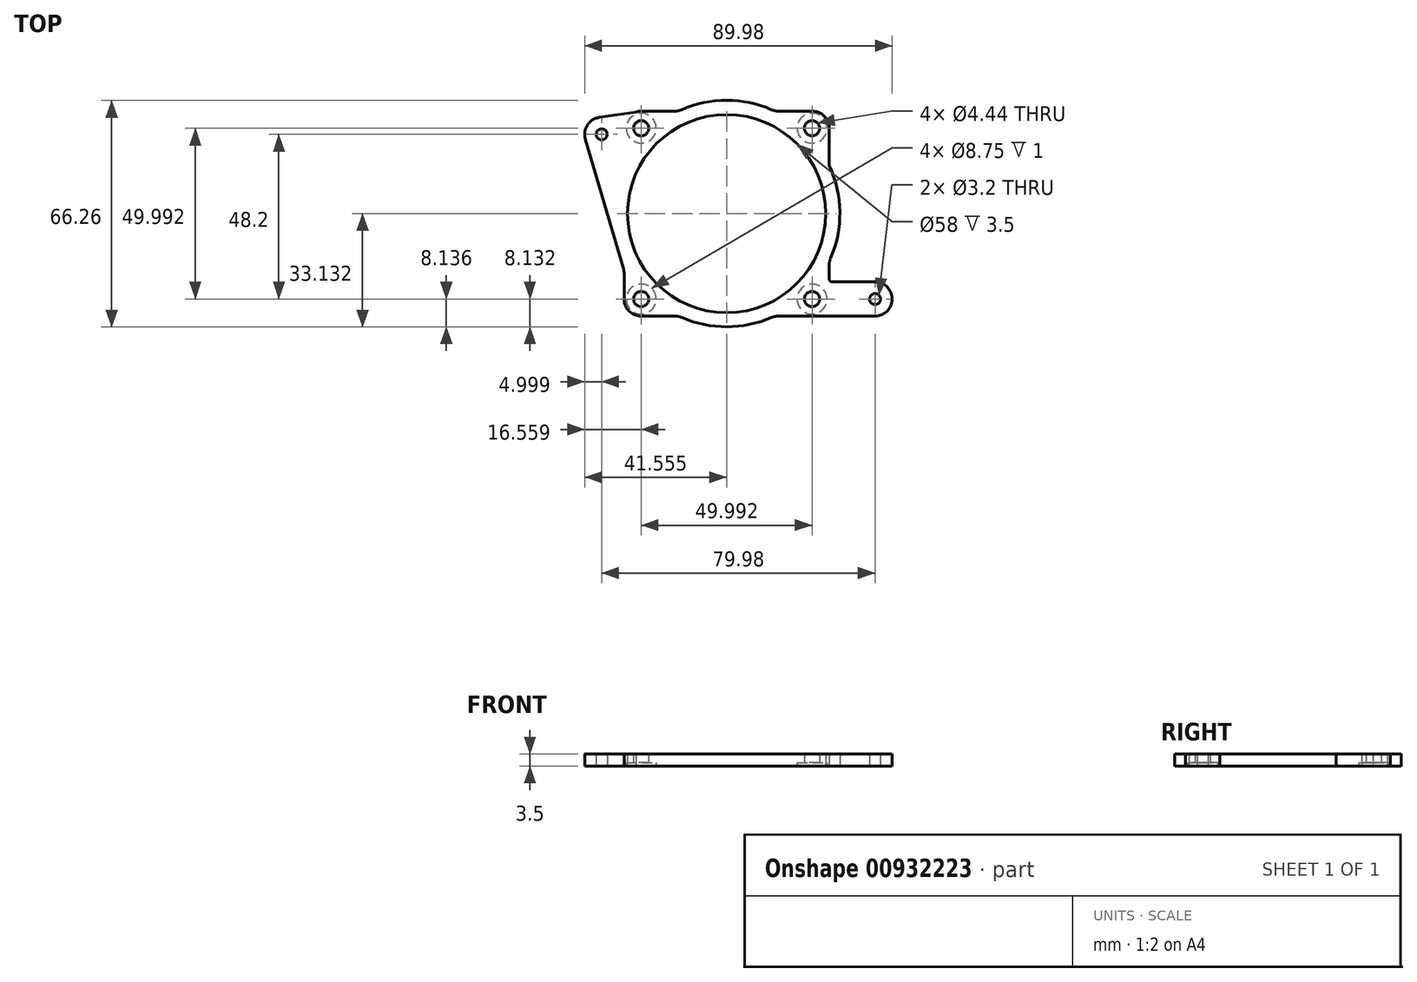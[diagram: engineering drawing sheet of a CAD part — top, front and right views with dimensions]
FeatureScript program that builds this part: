
annotation { "Feature Type Name" : "Feature", "Feature Type Description" : "" }
export const myFeature = defineFeature(function(context is Context, id is Id, definition is map)
    precondition{}
    {
        {
            var Q0;
            Q0=qCreatedBy(makeId("Top.planeOp"),FACE);
            var sketch = newSketch(context, id + "F0", { "sketchPlane" : qUnion([Q0])});
            skLineSegment(sketch, "E0.bottom", {"start": v(-53.42, 44.82) * mm, "end": v(48.18, 44.82) * mm, "construction": true});
            skLineSegment(sketch, "E0.top", {"start": v(-53.42, -8.48) * mm, "end": v(48.18, -8.48) * mm, "construction": true});
            skLineSegment(sketch, "E0.left", {"start": v(-53.42, 44.82) * mm, "end": v(-53.42, -8.48) * mm, "construction": true});
            skLineSegment(sketch, "E0.right", {"start": v(48.18, 44.82) * mm, "end": v(48.18, -8.48) * mm, "construction": true});
            skCircle(sketch, "E1", {"center": v(-39.42, -5.98) * mm, "radius": 1.6 * mm, "construction": true});
            skCircle(sketch, "E2", {"center": v(-38.12, 42.22) * mm, "radius": 1.6 * mm});
            skCircle(sketch, "E3", {"center": v(36.78, 42.22) * mm, "radius": 1.6 * mm, "construction": true});
            skCircle(sketch, "E4", {"center": v(41.86, -5.98) * mm, "radius": 1.6 * mm});
            skCircle(sketch, "E5", {"center": v(12.68, -0.88) * mm, "radius": 1.6 * mm, "construction": true});
            skCircle(sketch, "E6", {"center": v(12.68, 27.02) * mm, "radius": 1.6 * mm, "construction": true});
            skLineSegment(sketch, "E7.bottom", {"start": v(-26.56, 49.02) * mm, "end": v(-16.7, 49.02) * mm});
            skLineSegment(sketch, "E7.top", {"start": v(-26.56, -10.98) * mm, "end": v(-16.7, -10.98) * mm});
            skLineSegment(sketch, "E7.left", {"start": v(-31.56, 1.62) * mm, "end": v(-31.56, -5.98) * mm});
            skLineSegment(sketch, "E7.right", {"start": v(28.44, 44.02) * mm, "end": v(28.44, 33.08) * mm});
            skCircle(sketch, "E8", {"center": v(-26.56, 44.02) * mm, "radius": 2.22 * mm});
            skLineSegment(sketch, "E9", {"start": v(-31.56, 49.02) * mm, "end": v(28.44, -10.98) * mm, "construction": true});
            skLineSegment(sketch, "E10", {"start": v(28.44, 49.02) * mm, "end": v(-31.56, -10.98) * mm, "construction": true});
            skArc(sketch, "E11", {"start": v(-22.35, 44.82) * mm, "mid": v(-34.66, 17.59) * mm, "end": v(-20.04, -8.48) * mm, "construction": true});
            skCircle(sketch, "E12", {"center": v(23.43, 44.02) * mm, "radius": 2.22 * mm});
            skCircle(sketch, "E13", {"center": v(23.43, -5.97) * mm, "radius": 2.22 * mm});
            skCircle(sketch, "E14", {"center": v(-26.56, -5.97) * mm, "radius": 2.22 * mm});
            skPoint(sketch, "E15.visualSharp", {"position": v(28.44, 49.02) * mm});
            skArc(sketch, "E15.filletArc", {"start": v(28.44, 44.02) * mm, "mid": v(26.97, 47.56) * mm, "end": v(23.44, 49.02) * mm});
            skPoint(sketch, "E16.visualSharp", {"position": v(28.44, -10.98) * mm});
            skLineSegment(sketch, "E16.filletArc", {"start": v(23.44, -10.98) * mm, "end": v(23.44, -10.98) * mm});
            skPoint(sketch, "E17.visualSharp", {"position": v(-31.56, -10.98) * mm});
            skArc(sketch, "E17.filletArc", {"start": v(-31.56, -5.98) * mm, "mid": v(-30.1, -9.51) * mm, "end": v(-26.56, -10.98) * mm});
            skPoint(sketch, "E18.visualSharp", {"position": v(-31.56, 49.02) * mm});
            skArc(sketch, "E18.filletArc", {"start": v(-26.56, 49.02) * mm, "mid": v(-28.48, 48.64) * mm, "end": v(-30.1, 47.56) * mm});
            skPoint(sketch, "E19.19", {"position": v(-146.14, 42.5) * mm});
            skPoint(sketch, "E20.0", {"position": v(-66.16, -5.7) * mm});
            skPoint(sketch, "E21", {"position": v(-1.56, 17.8) * mm});
            skCircle(sketch, "E22", {"center": v(-1.56, 19.02) * mm, "radius": 29 * mm});
            skArc(sketch, "E23", {"start": v(-38.87, 47.17) * mm, "mid": v(-42.34, 44.9) * mm, "end": v(-42.92, 40.8) * mm});
            skLineSegment(sketch, "E24", {"start": v(-31.77, 3.04) * mm, "end": v(-42.92, 40.8) * mm});
            skLineSegment(sketch, "E25", {"start": v(-26.56, 49.02) * mm, "end": v(-38.87, 47.17) * mm});
            skLineSegment(sketch, "E26", {"start": v(41.86, -10.98) * mm, "end": v(23.44, -10.98) * mm});
            skPoint(sketch, "E27.visualSharp", {"position": v(46.86, 15.79) * mm});
            skLineSegment(sketch, "E28", {"start": v(37.65, 11.98) * mm, "end": v(37.65, 37.31) * mm, "construction": true});
            skLineSegment(sketch, "E29", {"start": v(37.65, 11.98) * mm, "end": v(37.65, -33.07) * mm, "construction": true});
            skArc(sketch, "E30.filletArc", {"start": v(-31.56, 1.62) * mm, "mid": v(-31.62, 2.33) * mm, "end": v(-31.77, 3.04) * mm});
            skArc(sketch, "E31.trimOffspring", {"start": v(37.53, -8.48) * mm, "mid": v(37.59, -8.58) * mm, "end": v(37.65, -8.67) * mm});
            skPoint(sketch, "E32.orphan", {"position": v(28.44, -5.98) * mm});
            skPoint(sketch, "E33.visualSharp", {"position": v(28.44, 35.44) * mm});
            skArc(sketch, "E34.trimOffspring", {"start": v(11.58, 49.43) * mm, "mid": v(-1.56, 52.15) * mm, "end": v(-14.71, 49.43) * mm});
            skArc(sketch, "E35.trimOffspring", {"start": v(-14.71, -11.39) * mm, "mid": v(-1.56, -14.1) * mm, "end": v(11.58, -11.39) * mm});
            skArc(sketch, "E36.trimOffspring", {"start": v(16.91, -8.48) * mm, "mid": v(21.2, -5.06) * mm, "end": v(24.85, -0.98) * mm, "construction": true});
            skLineSegment(sketch, "E37.trimOffspring", {"start": v(13.56, 49.02) * mm, "end": v(23.44, 49.02) * mm});
            skPoint(sketch, "E38.visualSharp", {"position": v(-15.62, 49.02) * mm});
            skArc(sketch, "E38.filletArc", {"start": v(-16.7, 49.02) * mm, "mid": v(-15.68, 49.13) * mm, "end": v(-14.71, 49.43) * mm});
            skPoint(sketch, "E39.visualSharp", {"position": v(12.5, 49.02) * mm});
            skArc(sketch, "E39.filletArc", {"start": v(11.58, 49.43) * mm, "mid": v(12.55, 49.13) * mm, "end": v(13.56, 49.02) * mm});
            skLineSegment(sketch, "E40.trimOffspring", {"start": v(13.56, -10.98) * mm, "end": v(23.44, -10.98) * mm});
            skPoint(sketch, "E41.visualSharp", {"position": v(-15.62, -10.98) * mm});
            skArc(sketch, "E41.filletArc", {"start": v(-14.71, -11.39) * mm, "mid": v(-15.68, -11.08) * mm, "end": v(-16.7, -10.98) * mm});
            skPoint(sketch, "E42.visualSharp", {"position": v(12.5, -10.98) * mm});
            skArc(sketch, "E42.filletArc", {"start": v(13.56, -10.98) * mm, "mid": v(12.55, -11.08) * mm, "end": v(11.58, -11.39) * mm});
            skCircle(sketch, "E43.converted", {"center": v(41.86, -5.98) * mm, "radius": 5 * mm});
            skLineSegment(sketch, "E44", {"start": v(41.86, -0.98) * mm, "end": v(29.44, -0.98) * mm});
            skLineSegment(sketch, "E45", {"start": v(24.85, -0.98) * mm, "end": v(24.85, -0.98) * mm});
            skLineSegment(sketch, "E46", {"start": v(28.44, 3.9) * mm, "end": v(28.44, 0.02) * mm});
            skArc(sketch, "E47.trimOffspring", {"start": v(28.85, 5.88) * mm, "mid": v(30.6, 26.97) * mm, "end": v(19.22, 44.82) * mm});
            skPoint(sketch, "E48.visualSharp", {"position": v(28.44, -0.98) * mm});
            skArc(sketch, "E48.filletArc", {"start": v(28.44, 0.02) * mm, "mid": v(28.73, -0.69) * mm, "end": v(29.44, -0.98) * mm});
            skPoint(sketch, "E49.visualSharp", {"position": v(28.44, 4.96) * mm});
            skArc(sketch, "E49.filletArc", {"start": v(28.85, 5.88) * mm, "mid": v(28.54, 4.9) * mm, "end": v(28.44, 3.9) * mm});
            skSolve(sketch);
        }
        {
            var Q0;
            Q0=qCreatedBy(makeId("Top.planeOp"),FACE);
            cPlane(context, id + "F1", {"entities" : qUnion([Q0]), "cplaneType" : CPlaneType.OFFSET, "offset" : 5 * mm, "oppositeDirection" : true, "width" : 150 * mm, "height" : 150 * mm});
        }
        {
            var Q0;
            Q0 = qSketchRegion(id + "F0", true);
            extrude(context, id + "F2", {"entities" : qUnion([Q0]), "depth" : 3.5 * mm, "offsetDistance" : 25 * mm});
        }
        {
            var Q0;
            Q0=makeQuery(id+"F2.opExtrude","CAP_FACE",FACE,{"disambiguationData":[OSD([sQuery(id+"F0.wireOp",EDGE,"E2"),sQuery(id+"F0.wireOp",EDGE,"E4"),sQuery(id+"F0.wireOp",EDGE,"E7.bottom"),sQuery(id+"F0.wireOp",EDGE,"E7.top"),sQuery(id+"F0.wireOp",EDGE,"E7.left"),sQuery(id+"F0.wireOp",EDGE,"E7.right"),sQuery(id+"F0.wireOp",EDGE,"E8"),sQuery(id+"F0.wireOp",EDGE,"E12"),sQuery(id+"F0.wireOp",EDGE,"E13"),sQuery(id+"F0.wireOp",EDGE,"E14"),sQuery(id+"F0.wireOp",EDGE,"E15.filletArc"),sQuery(id+"F0.wireOp",EDGE,"E17.filletArc"),sQuery(id+"F0.wireOp",EDGE,"E18.filletArc"),sQuery(id+"F0.wireOp",EDGE,"E22"),sQuery(id+"F0.wireOp",EDGE,"E23"),sQuery(id+"F0.wireOp",EDGE,"curC7CVh-JOHb-7Mg7-MYZK-eGtlUkxcjdBB"),sQuery(id+"F0.wireOp",EDGE,"E24"),sQuery(id+"F0.wireOp",EDGE,"E25"),sQuery(id+"F0.wireOp",EDGE,"E26"),sQuery(id+"F0.wireOp",EDGE,"FxnBB36o-Rqyz-MdkS-9HdU-SdkZIjoqN9XQ"),sQuery(id+"F0.wireOp",EDGE,"PDu09gB8-Ofy4-FQeL-J0Lt-99pAvs8q4Kbb"),sQuery(id+"F0.wireOp",EDGE,"E27.filletArc"),sQuery(id+"F0.wireOp",EDGE,"gc8W9cHn-Bc5P-Qay7-8Ruc-CuvNxYl3HCNp"),sQuery(id+"F0.wireOp",EDGE,"KVewsBho-RE48-E0Hx-cDzr-HIZNmGF8zBQT"),sQuery(id+"F0.wireOp",EDGE,"5kwrPDOV-29eI-Kryb-Ag34-BUCpRlZNhAOB"),sQuery(id+"F0.wireOp",EDGE,"dNwue7Wm-2wzY-Y4re-vDyQ-YOXkvpwNrZ5r"),sQuery(id+"F0.wireOp",EDGE,"E30.filletArc"),sQuery(id+"F0.wireOp",EDGE,"E33.filletArc")])],"isStart":true});
            var sketch = newSketch(context, id + "F3", { "sketchPlane" : qUnion([Q0])});
            skCircle(sketch, "E50.0", {"center": v(-26.56, 5.97) * mm, "radius": 2.22 * mm});
            skCircle(sketch, "E50.1", {"center": v(23.43, 5.97) * mm, "radius": 2.22 * mm});
            skCircle(sketch, "E50.2", {"center": v(23.43, -44.02) * mm, "radius": 2.22 * mm});
            skCircle(sketch, "E50.3", {"center": v(-26.56, -44.02) * mm, "radius": 2.22 * mm});
            skCircle(sketch, "E51", {"center": v(23.43, 5.97) * mm, "radius": 4.38 * mm});
            skCircle(sketch, "E52", {"center": v(-26.56, 5.97) * mm, "radius": 4.38 * mm});
            skCircle(sketch, "E53", {"center": v(-26.56, -44.02) * mm, "radius": 4.38 * mm});
            skCircle(sketch, "E54", {"center": v(23.43, -44.02) * mm, "radius": 4.38 * mm});
            skSolve(sketch);
        }
        {
            var Q0;
            Q0=makeQuery(id+"F3.imprint","IMPRINT",FACE,{"disambiguationData":[TD([[makeQuery(id+"F3.imprint","IMPRINT",EDGE,{"derivedFrom":sQuery(id+"F3.wireOp",EDGE,"E50.2")}),1.0]])]});
            var Q1;
            Q1=makeQuery(id+"F3.imprint","IMPRINT",FACE,{"disambiguationData":[TD([[makeQuery(id+"F3.imprint","IMPRINT",EDGE,{"derivedFrom":sQuery(id+"F3.wireOp",EDGE,"E50.3")}),1.0]])]});
            var Q2;
            Q2=makeQuery(id+"F3.imprint","IMPRINT",FACE,{"disambiguationData":[TD([[makeQuery(id+"F3.imprint","IMPRINT",EDGE,{"derivedFrom":sQuery(id+"F3.wireOp",EDGE,"E50.1")}),1.0]])]});
            var Q3;
            Q3=makeQuery(id+"F3.imprint","IMPRINT",FACE,{"disambiguationData":[TD([[makeQuery(id+"F3.imprint","IMPRINT",EDGE,{"derivedFrom":sQuery(id+"F3.wireOp",EDGE,"E50.0")}),1.0]])]});
            extrude(context, id + "F4", {"entities" : qUnion([Q0, Q1, Q2, Q3]), "operationType" : NewBodyOperationType.REMOVE, "oppositeDirection" : true, "depth" : 1 * mm, "offsetDistance" : 25 * mm});
        }
    });
